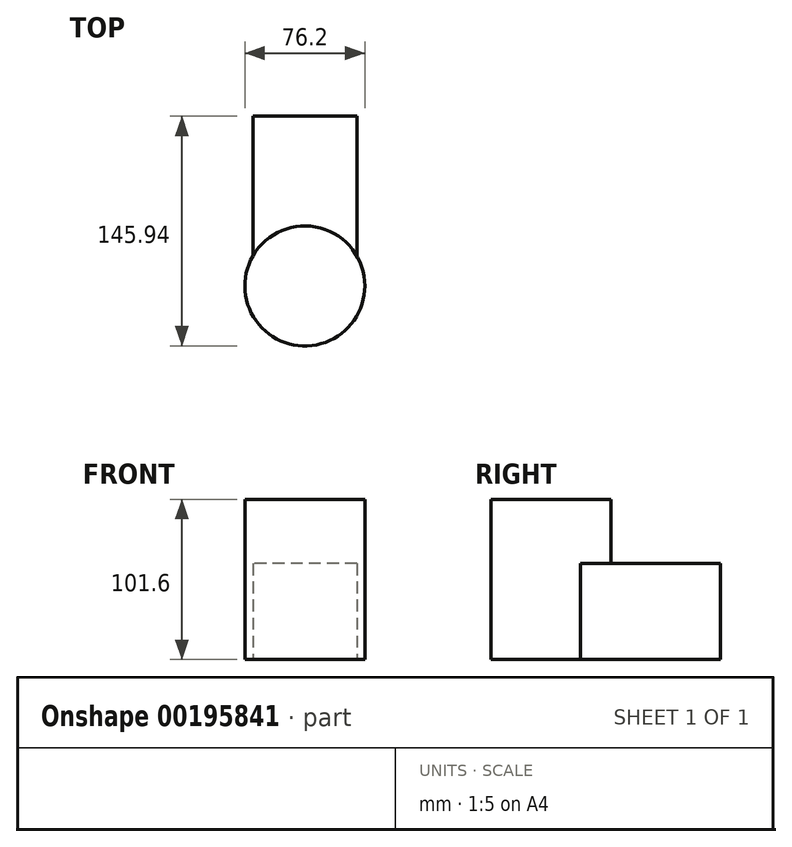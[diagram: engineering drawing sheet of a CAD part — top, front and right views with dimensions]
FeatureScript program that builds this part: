
annotation { "Feature Type Name" : "Feature", "Feature Type Description" : "" }
export const myFeature = defineFeature(function(context is Context, id is Id, definition is map)
    precondition{}
    {
        {
            var Q0;
            Q0=qCreatedBy(makeId("Top.planeOp"),FACE);
            var sketch = newSketch(context, id + "F0", { "sketchPlane" : qUnion([Q0])});
            skCircle(sketch, "E0", {"center": v(-29.09, -18.94) * mm, "radius": 38.1 * mm});
            skLineSegment(sketch, "E1.bottom", {"start": v(3.97, 0) * mm, "end": v(-62.07, 0) * mm});
            skLineSegment(sketch, "E1.top", {"start": v(3.97, 88.9) * mm, "end": v(-62.07, 88.9) * mm});
            skLineSegment(sketch, "E1.left", {"start": v(3.97, 0) * mm, "end": v(3.97, 88.9) * mm});
            skLineSegment(sketch, "E1.right", {"start": v(-62.07, 0) * mm, "end": v(-62.07, 88.9) * mm});
            skSolve(sketch);
        }
        {
            var Q0;
            {var subQ4=sQuery(id+"F0.wireOp",EDGE,"E1.top");Q0=makeQuery(id+"F0.imprint","IMPRINT",FACE,{"disambiguationData":[TD([[makeQuery(id+"F0.imprint","IMPRINT",EDGE,{"derivedFrom":subQ4}),1.0]])]});}
            extrude(context, id + "F1", {"entities" : qUnion([Q0]), "depth" : 60.96 * mm});
        }
        {
            var Q0;
            {var subQ0=sQuery(id+"F0.wireOp",EDGE,"E1.bottom");Q0=makeQuery(id+"F0.imprint","IMPRINT",FACE,{"disambiguationData":[TD([[makeQuery(id+"F0.imprint","IMPRINT",EDGE,{"derivedFrom":subQ0}),1.0]])]});}
            var Q1;
            {var subQ0=sQuery(id+"F0.wireOp",EDGE,"E1.bottom");Q1=makeQuery(id+"F0.imprint","IMPRINT",FACE,{"disambiguationData":[TD([[makeQuery(id+"F0.imprint","IMPRINT",EDGE,{"derivedFrom":subQ0}),-1.0]])]});}
            extrude(context, id + "F2", {"entities" : qUnion([Q0, Q1]), "operationType" : NewBodyOperationType.ADD, "depth" : 101.6 * mm});
        }
    });
